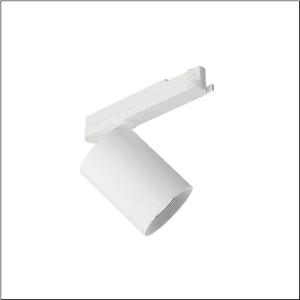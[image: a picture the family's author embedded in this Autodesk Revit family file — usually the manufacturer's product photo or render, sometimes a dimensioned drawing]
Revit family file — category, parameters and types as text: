
# Revit family: spot_21_51se13dba5b
name_source: partatom
category: Lighting Fixtures
units: mm (PartAtom-declared; Revit-internal decimal feet)

## family parameters
Cut with Voids When Loaded = No
Host = Face
Light Source = No
Part Type = Normal
Room Calculation Point = No
Round Connector Dimension = Use Diameter
Shared = No

## types (1)
- --- (1 x LED, 5190 lm, 42.4 W, 2700K)
    Apparent Load = 42 VA
    CIE Flux Codes = 95 98 99 100 100
    Color Rendering = 90
    Color Temperature = 2700K
    Default Elevation = 1800 mm
    Description = Spot 21, directional spotlight, light control with lens, of PMMA, LED rated luminous flux: 4.960lm, light colour: 927, control gear: ECG Multilumen, with 3-phase adapter, mains connection: 220..240V, AC, 50/60Hz, of aluminium, traffic white (RAL 9016), length: 253mm, diameter: 105mm, protection rating (complete): IP20, insulation class (complete): insulation class I (protective earthing), certification: CE, impact resistance: IK02, permissible ambient temperature for indoor applications: -20..+40°C, packaging unit: 1 piece
    Height = 175 mm
    Lamp = 1 x LED
    Lamp Light Flux = 5190 lm
    Lamp Power = 42.4 W
    Lamp count = 1
    Length = 105 mm
    Luminous efficacy = 122 lm/W
    Manufacturer = Siteco
    ModVariant = No
    Model = 51SE13DBA5B
    Mounting Place = Ceiling
    Mounting Type = Pendant
    Number of Poles = 1
    OnlyDefault = Yes
    Power Factor = 1
    Product Name = Spot 21
    Product group = directional spotlight
    ProductGroupID = 905
    Protection Class = Protection class I
    Protection Degree = IP 20
    RLX_Detail_Level = 1
    RLX_Emergency_Light_Flux = 0 lm
    RLX_Emergency_Type = 0
    RLX_Emergency_Type_DB = No
    RlxData = <blob elided: 17601 chars, md5=f2ead176>
    Socket = socket
    Standby Power = 0 W
    System Light Flux = 5190 lm
    System Power = 42 W
    Type Comments = factory setting: luminous flux: 100 % | (ON | ON | ON | ON) | 1050 mA
    Type Image = l_1003976.jpg
    URL = http://relux.com
    VarID = @adj_093233
    Voltage = 0 V
    Weight = 0.00 kg
    Width = 0 mm  [stored 0 ft]

note: [stored X ft] marks values corroborated as IEEE doubles in the binary element streams (Revit-internal decimal feet)

## geometry (parser evidence)
native form markers: Blend x4, Sweep x9
no freeform markers — native parametric forms only
